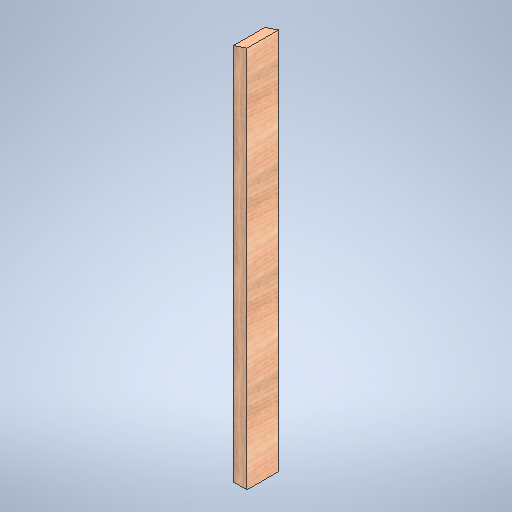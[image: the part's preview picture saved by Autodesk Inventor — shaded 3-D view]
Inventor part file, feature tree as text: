
AUTODESK INVENTOR PART (.ipt)
format: ipt  version: 2025.1 (Build 291241020, 241B)  size: 312,832 bytes
history: native  units: in
note: dims shown in document units (in); Inventor stores cm internally (conversion verified against a paired STEP export)
features: extrude x1, sketch x1
ambient origin geometry x8: Origin, YZ Plane, XZ Plane, XY Plane, X Axis, Y Axis, Z Axis, Center Point
bodies: Solid1 (feature_tree)
feature tree (2):
  extrude  "Extrusion1"  Depth=3.5in TaperAngle=0.0deg
  sketch  "Sketch1"  dims[d2=1.5in d3=3.5in d4=0.0in d5=42.0in d6=42.5in]
